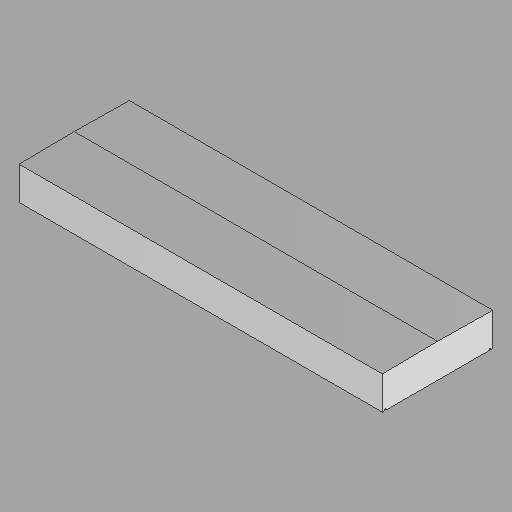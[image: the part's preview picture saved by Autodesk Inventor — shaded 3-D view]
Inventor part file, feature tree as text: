
AUTODESK INVENTOR PART (.ipt)
format: ipt  version: 2022.2 (Build 262287010, 287A)  size: 154,624 bytes
history: native  units: in
note: dims shown in document units (in); Inventor stores cm internally (conversion verified against a paired STEP export)
features: delete_face x3, extrude x2, other x2, thicken_offset x1, sketch x1, projected_geometry x1
ambient origin geometry x8: Origin, YZ Plane, XZ Plane, XY Plane, X Axis, Y Axis, Z Axis, Center Point
bodies: Solid1 (feature_tree), Solid2 (feature_tree)
feature tree (10):
  thicken_offset  "Thicken1"
  sketch  "Sketch1"  dims[d0=11.0in d1=11.0in d2=0.25in d3=0.25in d4=0.375in d5=0.25in d6=0.25in d7=0.375in d8=0.125in d9=0.0in d10=0.0in d11=65.873in d12=0.0in]
  extrude  "Extrusion1"  Depth=65.873in
  extrude  "Extrusion2"  Depth=0.25in
  delete_face  "Delete Face1"
  delete_face  "Delete Face2"
  delete_face  "Delete Face3"
  projected_geometry  "Projected Loop1"
  other  "Cap (5) (2)"
  other  "Cap (5) (2):1"
